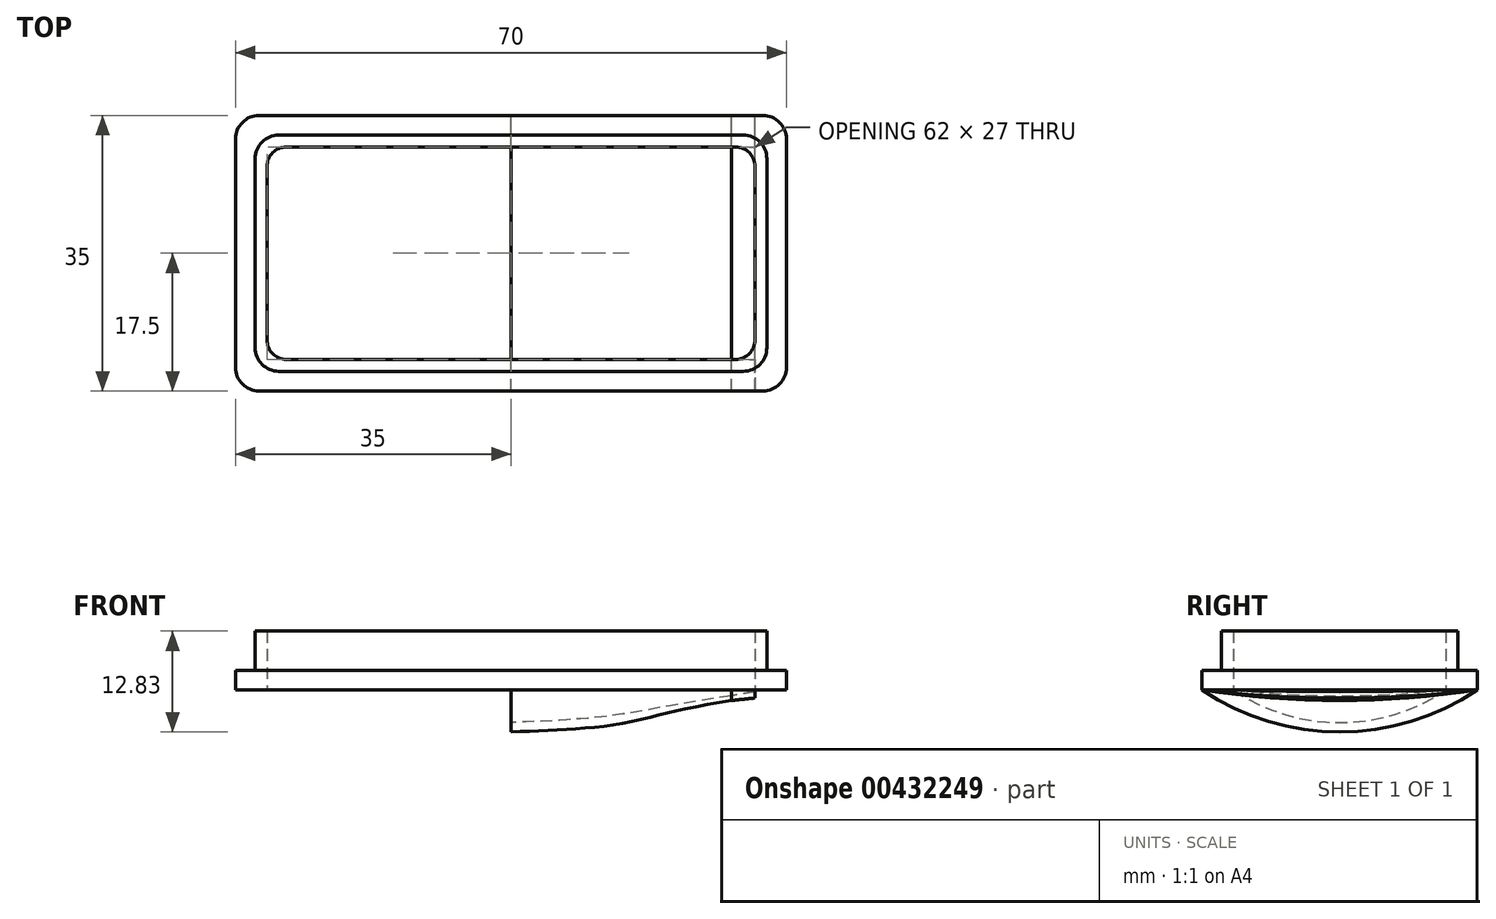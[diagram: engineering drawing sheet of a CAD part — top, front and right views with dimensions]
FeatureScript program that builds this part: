
annotation { "Feature Type Name" : "Feature", "Feature Type Description" : "" }
export const myFeature = defineFeature(function(context is Context, id is Id, definition is map)
    precondition{}
    {
        {
            var Q0;
            Q0=qCreatedBy(makeId("Top.planeOp"),FACE);
            var sketch = newSketch(context, id + "F0", { "sketchPlane" : qUnion([Q0])});
            skLineSegment(sketch, "E0.bottom", {"start": v(35, -17.5) * mm, "end": v(-35, -17.5) * mm});
            skLineSegment(sketch, "E0.top", {"start": v(35, 17.5) * mm, "end": v(-35, 17.5) * mm});
            skLineSegment(sketch, "E0.left", {"start": v(35, -17.5) * mm, "end": v(35, 17.5) * mm});
            skLineSegment(sketch, "E0.right", {"start": v(-35, -17.5) * mm, "end": v(-35, 17.5) * mm});
            skPoint(sketch, "E0.middle", {"position": v(0, 0) * mm});
            skPoint(sketch, "E1.left.end.orphan", {"position": v(32.5, 15) * mm});
            skPoint(sketch, "E2.left.end.orphan", {"position": v(31, 13.5) * mm});
            skPoint(sketch, "E2.bottom.start.orphan", {"position": v(31, -13.5) * mm});
            skPoint(sketch, "E1.bottom.start.orphan", {"position": v(32.5, -15) * mm});
            skPoint(sketch, "E2.right.end.orphan", {"position": v(-31, 13.5) * mm});
            skPoint(sketch, "E2.right.start.orphan", {"position": v(-31, -13.5) * mm});
            skPoint(sketch, "E1.right.end.orphan", {"position": v(-32.5, 15) * mm});
            skPoint(sketch, "E1.right.start.orphan", {"position": v(-32.5, -15) * mm});
            skSolve(sketch);
        }
        {
            var Q0;
            Q0=makeQuery(id+"F0.imprint","IMPRINT",FACE,{"disambiguationData":[TD([[makeQuery(id+"F0.imprint","IMPRINT",EDGE,{"derivedFrom":sQuery(id+"F0.wireOp",EDGE,"E0.bottom")}),-1.0]])]});
            extrude(context, id + "F1", {"entities" : qUnion([Q0]), "depth" : 2.5 * mm});
        }
        {
            var Q0;
            Q0=makeQuery(id+"F1.opExtrude","CAP_FACE",FACE,{"disambiguationData":[OSD([sQuery(id+"F0.wireOp",EDGE,"E0.bottom"),sQuery(id+"F0.wireOp",EDGE,"E0.top"),sQuery(id+"F0.wireOp",EDGE,"E0.left"),sQuery(id+"F0.wireOp",EDGE,"E0.right")])],"isStart":false});
            var sketch = newSketch(context, id + "F2", { "sketchPlane" : qUnion([Q0])});
            skLineSegment(sketch, "E3.bottom", {"start": v(31, -13.5) * mm, "end": v(-31, -13.5) * mm});
            skLineSegment(sketch, "E3.top", {"start": v(31, 13.5) * mm, "end": v(-31, 13.5) * mm});
            skLineSegment(sketch, "E3.left", {"start": v(31, -13.5) * mm, "end": v(31, 13.5) * mm});
            skLineSegment(sketch, "E3.right", {"start": v(-31, -13.5) * mm, "end": v(-31, 13.5) * mm});
            skPoint(sketch, "E3.middle", {"position": v(0, 0) * mm});
            skLineSegment(sketch, "E4.bottom", {"start": v(32.5, -15) * mm, "end": v(-32.5, -15) * mm});
            skLineSegment(sketch, "E4.top", {"start": v(32.5, 15) * mm, "end": v(-32.5, 15) * mm});
            skLineSegment(sketch, "E4.left", {"start": v(32.5, -15) * mm, "end": v(32.5, 15) * mm});
            skLineSegment(sketch, "E4.right", {"start": v(-32.5, -15) * mm, "end": v(-32.5, 15) * mm});
            skSolve(sketch);
        }
        {
            var Q0;
            Q0=makeQuery(id+"F2.imprint","IMPRINT",FACE,{"disambiguationData":[TD([[makeQuery(id+"F2.imprint","IMPRINT",EDGE,{"derivedFrom":sQuery(id+"F2.wireOp",EDGE,"E3.bottom")}),1.0]])]});
            extrude(context, id + "F3", {"entities" : qUnion([Q0]), "operationType" : NewBodyOperationType.ADD, "depth" : 5 * mm});
        }
        {
            var Q0;
            Q0=makeQuery(id+"F3.boolean.opBoolean","SPLIT",FACE,{"disambiguationData":[TD([makeQuery(id+"F3.opExtrude","SWEPT_FACE",FACE,{"disambiguationData":[OSD([sQuery(id+"F2.wireOp",EDGE,"E3.bottom")])]})])],"derivedFrom":makeQuery(id+"F1.opExtrude","CAP_FACE",FACE,{"disambiguationData":[OSD([sQuery(id+"F0.wireOp",EDGE,"E0.bottom"),sQuery(id+"F0.wireOp",EDGE,"E0.top"),sQuery(id+"F0.wireOp",EDGE,"E0.left"),sQuery(id+"F0.wireOp",EDGE,"E0.right")])],"isStart":false})});
            extrude(context, id + "F4", {"entities" : qUnion([Q0]), "operationType" : NewBodyOperationType.REMOVE, "endBound" : BoundingType.UP_TO_NEXT, "oppositeDirection" : true, "depth" : 25 * mm});
        }
        {
            var Q0;
            Q0=makeQuery(id+"F1.opExtrude","CAP_FACE",FACE,{"disambiguationData":[OSD([sQuery(id+"F0.wireOp",EDGE,"E0.bottom"),sQuery(id+"F0.wireOp",EDGE,"E0.top"),sQuery(id+"F0.wireOp",EDGE,"E0.left"),sQuery(id+"F0.wireOp",EDGE,"E0.right")])],"isStart":true});
            var sketch = newSketch(context, id + "F5", { "sketchPlane" : qUnion([Q0])});
            skLineSegment(sketch, "E5.bottom", {"start": v(31, -13.5) * mm, "end": v(-31, -13.5) * mm});
            skLineSegment(sketch, "E5.top", {"start": v(31, 13.5) * mm, "end": v(-31, 13.5) * mm});
            skLineSegment(sketch, "E5.left", {"start": v(31, -13.5) * mm, "end": v(31, 13.5) * mm});
            skLineSegment(sketch, "E5.right", {"start": v(-31, -13.5) * mm, "end": v(-31, 13.5) * mm});
            skPoint(sketch, "E5.middle", {"position": v(0, 0) * mm});
            skSolve(sketch);
        }
        {
            var Q0;
            Q0=qCreatedBy(makeId("Right.planeOp"),FACE);
            cPlane(context, id + "F6", {"entities" : qUnion([Q0]), "cplaneType" : CPlaneType.OFFSET, "offset" : 7 * mm, "width" : 150 * mm, "height" : 150 * mm});
        }
        {
            var Q0;
            Q0=qCreatedBy(makeId("Right.planeOp"),FACE);
            cPlane(context, id + "F7", {"entities" : qUnion([Q0]), "cplaneType" : CPlaneType.OFFSET, "offset" : 14 * mm, "width" : 150 * mm, "height" : 150 * mm});
        }
        {
            var Q0;
            Q0=qCreatedBy(makeId("Right.planeOp"),FACE);
            cPlane(context, id + "F8", {"entities" : qUnion([Q0]), "cplaneType" : CPlaneType.OFFSET, "offset" : 21 * mm, "width" : 150 * mm, "height" : 150 * mm});
        }
        {
            var Q0;
            Q0=qCreatedBy(makeId("Right.planeOp"),FACE);
            cPlane(context, id + "F9", {"entities" : qUnion([Q0]), "cplaneType" : CPlaneType.OFFSET, "offset" : 28 * mm, "width" : 150 * mm, "height" : 150 * mm});
        }
        {
            var Q0;
            Q0=qCreatedBy(makeId("Right.planeOp"),FACE);
            cPlane(context, id + "F10", {"entities" : qUnion([Q0]), "cplaneType" : CPlaneType.OFFSET, "offset" : 35 * mm, "width" : 150 * mm, "height" : 150 * mm});
        }
        {
            var Q0;
            Q0=qCreatedBy(id+"F6.planeOp",FACE);
            var sketch = newSketch(context, id + "F11", { "sketchPlane" : qUnion([Q0])});
            skArc(sketch, "E6", {"start": v(-17.5, 0) * mm, "mid": v(0, -4.99) * mm, "end": v(17.5, 0) * mm});
            skArc(sketch, "E7", {"start": v(-13.5, 0) * mm, "mid": v(0, -3.79) * mm, "end": v(13.5, 0) * mm});
            skLineSegment(sketch, "E8", {"start": v(-17.5, 0) * mm, "end": v(-13.5, 0) * mm});
            skLineSegment(sketch, "E9", {"start": v(13.5, 0) * mm, "end": v(17.5, 0) * mm});
            skSolve(sketch);
        }
        {
            var Q0;
            Q0=qCreatedBy(id+"F7.planeOp",FACE);
            var sketch = newSketch(context, id + "F12", { "sketchPlane" : qUnion([Q0])});
            skArc(sketch, "E10", {"start": v(-17.5, 0) * mm, "mid": v(0, -4.27) * mm, "end": v(17.5, 0) * mm});
            skArc(sketch, "E11", {"start": v(-13.5, 0) * mm, "mid": v(0, -3.07) * mm, "end": v(13.5, 0) * mm});
            skLineSegment(sketch, "E12", {"start": v(-17.5, 0) * mm, "end": v(-13.5, 0) * mm});
            skLineSegment(sketch, "E13", {"start": v(13.5, 0) * mm, "end": v(17.5, 0) * mm});
            skSolve(sketch);
        }
        {
            var Q0;
            Q0=qCreatedBy(id+"F8.planeOp",FACE);
            var sketch = newSketch(context, id + "F13", { "sketchPlane" : qUnion([Q0])});
            skArc(sketch, "E14", {"start": v(-17.5, 0) * mm, "mid": v(0, -2.64) * mm, "end": v(17.5, 0) * mm});
            skArc(sketch, "E15", {"start": v(-13.5, 0) * mm, "mid": v(0, -1.84) * mm, "end": v(13.5, 0) * mm});
            skLineSegment(sketch, "E16", {"start": v(-17.5, 0) * mm, "end": v(-13.5, 0) * mm});
            skLineSegment(sketch, "E17", {"start": v(13.5, 0) * mm, "end": v(17.5, 0) * mm});
            skSolve(sketch);
        }
        {
            var Q0;
            Q0=qCreatedBy(id+"F9.planeOp",FACE);
            var sketch = newSketch(context, id + "F14", { "sketchPlane" : qUnion([Q0])});
            skArc(sketch, "E18", {"start": v(-17.5, 0) * mm, "mid": v(0, -1.33) * mm, "end": v(17.5, 0) * mm});
            skArc(sketch, "E19", {"start": v(-13.5, 0) * mm, "mid": v(0, -0.73) * mm, "end": v(13.5, 0) * mm});
            skLineSegment(sketch, "E20", {"start": v(-17.5, 0) * mm, "end": v(-13.5, 0) * mm});
            skLineSegment(sketch, "E21", {"start": v(13.5, 0) * mm, "end": v(17.5, 0) * mm});
            skSolve(sketch);
        }
        {
            var Q0;
            Q0=qCreatedBy(id+"F10.planeOp",FACE);
            var sketch = newSketch(context, id + "F15", { "sketchPlane" : qUnion([Q0])});
            skLineSegment(sketch, "E22", {"start": v(-17.5, 0) * mm, "end": v(17.5, 0) * mm});
            skSolve(sketch);
        }
        {
            var Q0;
            Q0=qCreatedBy(makeId("Right.planeOp"),FACE);
            var sketch = newSketch(context, id + "F16", { "sketchPlane" : qUnion([Q0])});
            skArc(sketch, "E23", {"start": v(-17.5, 0) * mm, "mid": v(0, -5.33) * mm, "end": v(17.5, 0) * mm});
            skArc(sketch, "E24", {"start": v(-13.5, 0) * mm, "mid": v(0, -4.13) * mm, "end": v(13.5, 0) * mm});
            skLineSegment(sketch, "E25", {"start": v(-17.5, 0) * mm, "end": v(-13.5, 0) * mm});
            skLineSegment(sketch, "E26", {"start": v(13.5, 0) * mm, "end": v(17.5, 0) * mm});
            skSolve(sketch);
        }
        {
            var Q0;
            Q0=qCreatedBy(makeId("Right.planeOp"),FACE);
            cPlane(context, id + "F17", {"entities" : qUnion([Q0]), "cplaneType" : CPlaneType.OFFSET, "offset" : 31 * mm, "width" : 150 * mm, "height" : 150 * mm});
        }
        {
            var Q1;
            Q1=makeQuery(id+"F16.imprint","IMPRINT",FACE,{"disambiguationData":[TD([[makeQuery(id+"F16.imprint","IMPRINT",EDGE,{"derivedFrom":sQuery(id+"F16.wireOp",EDGE,"E23")}),1.0]])]});
            var Q2;
            Q2=makeQuery(id+"F11.imprint","IMPRINT",FACE,{"disambiguationData":[TD([[makeQuery(id+"F11.imprint","IMPRINT",EDGE,{"derivedFrom":sQuery(id+"F11.wireOp",EDGE,"E6")}),1.0]])]});
            var Q3;
            Q3=makeQuery(id+"F12.imprint","IMPRINT",FACE,{"disambiguationData":[TD([[makeQuery(id+"F12.imprint","IMPRINT",EDGE,{"derivedFrom":sQuery(id+"F12.wireOp",EDGE,"E10")}),1.0]])]});
            var Q4;
            Q4=makeQuery(id+"F13.imprint","IMPRINT",FACE,{"disambiguationData":[TD([[makeQuery(id+"F13.imprint","IMPRINT",EDGE,{"derivedFrom":sQuery(id+"F13.wireOp",EDGE,"E14")}),1.0]])]});
            var Q5;
            Q5=makeQuery(id+"F14.imprint","IMPRINT",FACE,{"disambiguationData":[TD([[makeQuery(id+"F14.imprint","IMPRINT",EDGE,{"derivedFrom":sQuery(id+"F14.wireOp",EDGE,"E18")}),1.0]])]});
            loft(context, id + "F18", {"sheetProfilesArray" : [{ "sheetProfileEntities" : qUnion([Q1]) }, { "sheetProfileEntities" : qUnion([Q2]) }, { "sheetProfileEntities" : qUnion([Q3]) }, { "sheetProfileEntities" : qUnion([Q4]) }, { "sheetProfileEntities" : qUnion([Q5]) }]});
        }
        {
            var Q0;
            Q0=qCreatedBy(id+"F17.planeOp",FACE);
            var sketch = newSketch(context, id + "F19", { "sketchPlane" : qUnion([Q0])});
            skLineSegment(sketch, "E27", {"start": v(13.5, 0) * mm, "end": v(-13.5, 0) * mm});
            skArc(sketch, "E28", {"start": v(-17.5, 0) * mm, "mid": v(0, -1) * mm, "end": v(17.5, 0) * mm});
            skLineSegment(sketch, "E29", {"start": v(-13.5, 0) * mm, "end": v(-17.5, 0) * mm});
            skLineSegment(sketch, "E30", {"start": v(13.5, 0) * mm, "end": v(17.5, 0) * mm});
            skArc(sketch, "E31", {"start": v(-13.5, 0) * mm, "mid": v(0, -0.2) * mm, "end": v(13.5, 0) * mm});
            skSolve(sketch);
        }
        {
            var Q0;
            Q0=makeQuery(id+"F1.opExtrude","SWEPT_EDGE",EDGE,{"disambiguationData":[OSD([sQuery(id+"F0.wireOp",EDGE,"E0.top"),sQuery(id+"F0.wireOp",EDGE,"E0.left")])]});
            var Q1;
            Q1=makeQuery(id+"F1.opExtrude","SWEPT_EDGE",EDGE,{"disambiguationData":[OSD([sQuery(id+"F0.wireOp",EDGE,"E0.bottom"),sQuery(id+"F0.wireOp",EDGE,"E0.left")])]});
            var Q2;
            Q2=makeQuery(id+"F1.opExtrude","SWEPT_EDGE",EDGE,{"disambiguationData":[OSD([sQuery(id+"F0.wireOp",EDGE,"E0.top"),sQuery(id+"F0.wireOp",EDGE,"E0.right")])]});
            var Q3;
            Q3=makeQuery(id+"F1.opExtrude","SWEPT_EDGE",EDGE,{"disambiguationData":[OSD([sQuery(id+"F0.wireOp",EDGE,"E0.bottom"),sQuery(id+"F0.wireOp",EDGE,"E0.right")])]});
            fillet(context, id + "F20", {"entities" : qUnion([Q0, Q1, Q2, Q3]), "radius" : 3 * mm, "tangentPropagation" : true, "allowEdgeOverflow" : false});
        }
        {
            var Q0;
            Q0=makeQuery(id+"F3.opExtrude","SWEPT_EDGE",EDGE,{"disambiguationData":[OSD([sQuery(id+"F2.wireOp",EDGE,"E4.bottom"),sQuery(id+"F2.wireOp",EDGE,"E4.left")])]});
            var Q1;
            Q1=makeQuery(id+"F3.opExtrude","SWEPT_EDGE",EDGE,{"disambiguationData":[OSD([sQuery(id+"F2.wireOp",EDGE,"E4.top"),sQuery(id+"F2.wireOp",EDGE,"E4.left")])]});
            var Q2;
            Q2=makeQuery(id+"F3.opExtrude","SWEPT_EDGE",EDGE,{"disambiguationData":[OSD([sQuery(id+"F2.wireOp",EDGE,"E4.bottom"),sQuery(id+"F2.wireOp",EDGE,"E4.right")])]});
            var Q3;
            Q3=makeQuery(id+"F3.opExtrude","SWEPT_EDGE",EDGE,{"disambiguationData":[OSD([sQuery(id+"F2.wireOp",EDGE,"E4.top"),sQuery(id+"F2.wireOp",EDGE,"E4.right")])]});
            fillet(context, id + "F21", {"entities" : qUnion([Q0, Q1, Q2, Q3]), "radius" : 3 * mm, "tangentPropagation" : true, "allowEdgeOverflow" : false});
        }
        {
            var Q0;
            {var subQ0=sQuery(id+"F2.wireOp",EDGE,"E3.right");var subQ1=sQuery(id+"F2.wireOp",EDGE,"E3.top");Q0=makeQuery(id+"F4.boolean.opBoolean","MERGE",EDGE,{"derivedFrom":[makeQuery(id+"F3.opExtrude","SWEPT_EDGE",EDGE,{"disambiguationData":[OSD([subQ1,subQ0])]})],"fromTools":[makeQuery(id+"F4.opExtrude","SWEPT_EDGE",EDGE,{"disambiguationData":[OSD([subQ1,subQ0])]})]});}
            var Q1;
            {var subQ0=sQuery(id+"F2.wireOp",EDGE,"E3.left");var subQ1=sQuery(id+"F2.wireOp",EDGE,"E3.top");Q1=makeQuery(id+"F4.boolean.opBoolean","MERGE",EDGE,{"derivedFrom":[makeQuery(id+"F3.opExtrude","SWEPT_EDGE",EDGE,{"disambiguationData":[OSD([subQ1,subQ0])]})],"fromTools":[makeQuery(id+"F4.opExtrude","SWEPT_EDGE",EDGE,{"disambiguationData":[OSD([subQ1,subQ0])]})]});}
            var Q2;
            {var subQ0=sQuery(id+"F2.wireOp",EDGE,"E3.left");var subQ1=sQuery(id+"F2.wireOp",EDGE,"E3.bottom");Q2=makeQuery(id+"F4.boolean.opBoolean","MERGE",EDGE,{"derivedFrom":[makeQuery(id+"F3.opExtrude","SWEPT_EDGE",EDGE,{"disambiguationData":[OSD([subQ1,subQ0])]})],"fromTools":[makeQuery(id+"F4.opExtrude","SWEPT_EDGE",EDGE,{"disambiguationData":[OSD([subQ1,subQ0])]})]});}
            var Q3;
            {var subQ0=sQuery(id+"F2.wireOp",EDGE,"E3.right");var subQ1=sQuery(id+"F2.wireOp",EDGE,"E3.bottom");Q3=makeQuery(id+"F4.boolean.opBoolean","MERGE",EDGE,{"derivedFrom":[makeQuery(id+"F3.opExtrude","SWEPT_EDGE",EDGE,{"disambiguationData":[OSD([subQ1,subQ0])]})],"fromTools":[makeQuery(id+"F4.opExtrude","SWEPT_EDGE",EDGE,{"disambiguationData":[OSD([subQ1,subQ0])]})]});}
            fillet(context, id + "F22", {"entities" : qUnion([Q0, Q1, Q2, Q3]), "radius" : 2.5 * mm, "tangentPropagation" : true, "allowEdgeOverflow" : false});
        }
        {
            var Q0;
            Q0=makeQuery(id+"F14.imprint","IMPRINT",FACE,{"disambiguationData":[TD([[makeQuery(id+"F14.imprint","IMPRINT",EDGE,{"derivedFrom":sQuery(id+"F14.wireOp",EDGE,"E18")}),1.0]])]});
            var Q1;
            Q1=makeQuery(id+"F19.imprint","IMPRINT",FACE,{"disambiguationData":[TD([[makeQuery(id+"F19.imprint","IMPRINT",EDGE,{"derivedFrom":sQuery(id+"F19.wireOp",EDGE,"E28")}),1.0]])]});
            loft(context, id + "F23", {"sheetProfilesArray" : [{ "sheetProfileEntities" : qUnion([Q0]) }, { "sheetProfileEntities" : qUnion([Q1]) }]});
        }
    });
